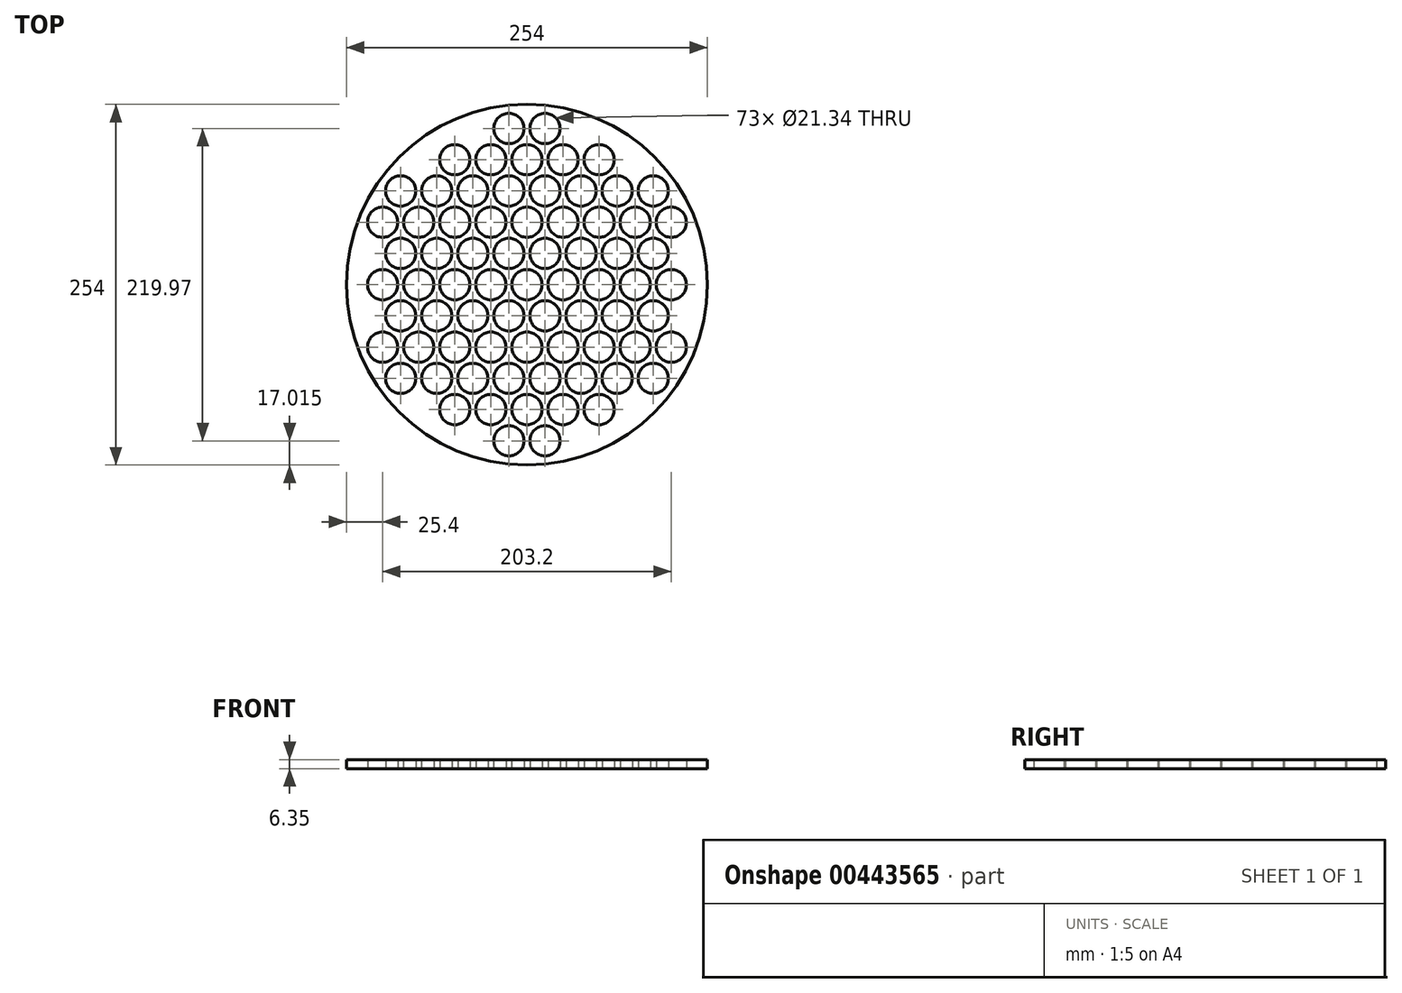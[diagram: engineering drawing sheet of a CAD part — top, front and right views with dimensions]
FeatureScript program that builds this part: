
annotation { "Feature Type Name" : "Feature", "Feature Type Description" : "" }
export const myFeature = defineFeature(function(context is Context, id is Id, definition is map)
    precondition{}
    {
        {
            var Q0;
            Q0=qCreatedBy(makeId("Top.planeOp"),FACE);
            var sketch = newSketch(context, id + "F0", { "sketchPlane" : qUnion([Q0])});
            skCircle(sketch, "E0", {"center": v(0, 0) * mm, "radius": 10.67 * mm});
            skCircle(sketch, "E1.1.0.0", {"center": v(25.4, 0) * mm, "radius": 10.67 * mm});
            skCircle(sketch, "E1.2.0.0", {"center": v(50.8, 0) * mm, "radius": 10.67 * mm});
            skLineSegment(sketch, "E1.direction1", {"start": v(0, 0) * mm, "end": v(25.4, 0) * mm, "construction": true});
            skCircle(sketch, "E2.0.3.0", {"center": v(76.2, 0) * mm, "radius": 10.67 * mm});
            skCircle(sketch, "E2.0.4.0", {"center": v(101.6, 0) * mm, "radius": 10.67 * mm});
            skCircle(sketch, "E3", {"center": v(12.7, 22) * mm, "radius": 10.67 * mm});
            skCircle(sketch, "E4.1.0.0", {"center": v(38.1, 22) * mm, "radius": 10.67 * mm});
            skCircle(sketch, "E4.2.0.0", {"center": v(63.5, 22) * mm, "radius": 10.67 * mm});
            skCircle(sketch, "E4.3.0.0", {"center": v(88.9, 22) * mm, "radius": 10.67 * mm});
            skLineSegment(sketch, "E4.direction1", {"start": v(12.7, 22) * mm, "end": v(38.1, 22) * mm, "construction": true});
            skCircle(sketch, "E5", {"center": v(0, 44) * mm, "radius": 10.67 * mm});
            skCircle(sketch, "E6.1.0.0", {"center": v(25.4, 44) * mm, "radius": 10.67 * mm});
            skCircle(sketch, "E6.2.0.0", {"center": v(50.8, 44) * mm, "radius": 10.67 * mm});
            skLineSegment(sketch, "E6.direction1", {"start": v(0, 44) * mm, "end": v(25.4, 44) * mm, "construction": true});
            skCircle(sketch, "E7.0.3.0", {"center": v(76.2, 44) * mm, "radius": 10.67 * mm});
            skCircle(sketch, "E7.0.4.0", {"center": v(101.6, 44) * mm, "radius": 10.67 * mm});
            skCircle(sketch, "E8", {"center": v(12.7, 66) * mm, "radius": 10.67 * mm});
            skCircle(sketch, "E9.1.0.0", {"center": v(38.1, 66) * mm, "radius": 10.67 * mm});
            skCircle(sketch, "E9.2.0.0", {"center": v(63.5, 66) * mm, "radius": 10.67 * mm});
            skCircle(sketch, "E9.3.0.0", {"center": v(88.9, 66) * mm, "radius": 10.67 * mm});
            skLineSegment(sketch, "E9.direction1", {"start": v(12.7, 66) * mm, "end": v(38.1, 66) * mm, "construction": true});
            skCircle(sketch, "E10", {"center": v(0, 0) * mm, "radius": 127 * mm});
            skCircle(sketch, "E11", {"center": v(0, 87.99) * mm, "radius": 10.67 * mm});
            skCircle(sketch, "E12.1.0.0", {"center": v(25.4, 87.99) * mm, "radius": 10.67 * mm});
            skCircle(sketch, "E12.2.0.0", {"center": v(50.8, 87.99) * mm, "radius": 10.67 * mm});
            skLineSegment(sketch, "E12.direction1", {"start": v(0, 87.99) * mm, "end": v(25.4, 87.99) * mm, "construction": true});
            skCircle(sketch, "E13", {"center": v(12.7, 109.99) * mm, "radius": 10.67 * mm});
            skLineSegment(sketch, "E14.direction1", {"start": v(12.7, 109.99) * mm, "end": v(38.1, 109.99) * mm, "construction": true});
            skCircle(sketch, "E15.MirrorC", {"center": v(-12.7, 66) * mm, "radius": 10.67 * mm});
            skLineSegment(sketch, "E16.MirrorCS", {"start": v(-12.7, 109.99) * mm, "end": v(-38.1, 109.99) * mm, "construction": true});
            skLineSegment(sketch, "E17.MirrorCS", {"start": v(-12.7, 66) * mm, "end": v(-38.1, 66) * mm, "construction": true});
            skCircle(sketch, "E18.MirrorC", {"center": v(-25.4, 87.99) * mm, "radius": 10.67 * mm});
            skCircle(sketch, "E19.MirrorC", {"center": v(-101.6, 44) * mm, "radius": 10.67 * mm});
            skCircle(sketch, "E20.MirrorC", {"center": v(-88.9, 66) * mm, "radius": 10.67 * mm});
            skCircle(sketch, "E21.MirrorC", {"center": v(-50.8, 87.99) * mm, "radius": 10.67 * mm});
            skLineSegment(sketch, "E22.MirrorCS", {"start": v(0, 44) * mm, "end": v(-25.4, 44) * mm, "construction": true});
            skCircle(sketch, "E23.MirrorC", {"center": v(-25.4, 44) * mm, "radius": 10.67 * mm});
            skCircle(sketch, "E24.MirrorC", {"center": v(-63.5, 66) * mm, "radius": 10.67 * mm});
            skCircle(sketch, "E25.MirrorC", {"center": v(-76.2, 44) * mm, "radius": 10.67 * mm});
            skLineSegment(sketch, "E26.MirrorCS", {"start": v(-12.7, 22) * mm, "end": v(-38.1, 22) * mm, "construction": true});
            skCircle(sketch, "E27.MirrorC", {"center": v(-25.4, 0) * mm, "radius": 10.67 * mm});
            skCircle(sketch, "E28.MirrorC", {"center": v(-38.1, 66) * mm, "radius": 10.67 * mm});
            skLineSegment(sketch, "E29.MirrorCS", {"start": v(0, 0) * mm, "end": v(-25.4, 0) * mm, "construction": true});
            skLineSegment(sketch, "E30.MirrorCS", {"start": v(0, 87.99) * mm, "end": v(-25.4, 87.99) * mm, "construction": true});
            skCircle(sketch, "E31.MirrorC", {"center": v(-38.1, 22) * mm, "radius": 10.67 * mm});
            skCircle(sketch, "E32.MirrorC", {"center": v(-76.2, 0) * mm, "radius": 10.67 * mm});
            skCircle(sketch, "E33.MirrorC", {"center": v(-50.8, 44) * mm, "radius": 10.67 * mm});
            skCircle(sketch, "E34.MirrorC", {"center": v(-101.6, 0) * mm, "radius": 10.67 * mm});
            skCircle(sketch, "E35.MirrorC", {"center": v(-50.8, 0) * mm, "radius": 10.67 * mm});
            skCircle(sketch, "E36.MirrorC", {"center": v(-12.7, 22) * mm, "radius": 10.67 * mm});
            skCircle(sketch, "E37.MirrorC", {"center": v(-12.7, 109.99) * mm, "radius": 10.67 * mm});
            skCircle(sketch, "E38.MirrorC", {"center": v(-63.5, 22) * mm, "radius": 10.67 * mm});
            skCircle(sketch, "E39.MirrorC", {"center": v(-88.9, 22) * mm, "radius": 10.67 * mm});
            skCircle(sketch, "E40.MirrorC", {"center": v(0, -87.99) * mm, "radius": 10.67 * mm});
            skLineSegment(sketch, "E41.MirrorCS", {"start": v(0, -44) * mm, "end": v(-25.4, -44) * mm, "construction": true});
            skCircle(sketch, "E42.MirrorC", {"center": v(0, -44) * mm, "radius": 10.67 * mm});
            skLineSegment(sketch, "E43.MirrorCS", {"start": v(0, -87.99) * mm, "end": v(-25.4, -87.99) * mm, "construction": true});
            skLineSegment(sketch, "E44.MirrorCS", {"start": v(-12.7, -66) * mm, "end": v(-38.1, -66) * mm, "construction": true});
            skCircle(sketch, "E45.MirrorC", {"center": v(12.7, -66) * mm, "radius": 10.67 * mm});
            skCircle(sketch, "E46.MirrorC", {"center": v(25.4, -87.99) * mm, "radius": 10.67 * mm});
            skCircle(sketch, "E47.MirrorC", {"center": v(-50.8, -87.99) * mm, "radius": 10.67 * mm});
            skLineSegment(sketch, "E48.MirrorCS", {"start": v(-12.7, -109.99) * mm, "end": v(-38.1, -109.99) * mm, "construction": true});
            skCircle(sketch, "E49.MirrorC", {"center": v(101.6, -44) * mm, "radius": 10.67 * mm});
            skCircle(sketch, "E50.MirrorC", {"center": v(-50.8, -44) * mm, "radius": 10.67 * mm});
            skCircle(sketch, "E51.MirrorC", {"center": v(-12.7, -66) * mm, "radius": 10.67 * mm});
            skCircle(sketch, "E52.MirrorC", {"center": v(76.2, -44) * mm, "radius": 10.67 * mm});
            skCircle(sketch, "E53.MirrorC", {"center": v(63.5, -22) * mm, "radius": 10.67 * mm});
            skCircle(sketch, "E54.MirrorC", {"center": v(-76.2, -44) * mm, "radius": 10.67 * mm});
            skCircle(sketch, "E55.MirrorC", {"center": v(50.8, -87.99) * mm, "radius": 10.67 * mm});
            skCircle(sketch, "E56.MirrorC", {"center": v(12.7, -22) * mm, "radius": 10.67 * mm});
            skCircle(sketch, "E57.MirrorC", {"center": v(38.1, -66) * mm, "radius": 10.67 * mm});
            skCircle(sketch, "E58.MirrorC", {"center": v(-38.1, -22) * mm, "radius": 10.67 * mm});
            skLineSegment(sketch, "E59.MirrorCS", {"start": v(12.7, -66) * mm, "end": v(38.1, -66) * mm, "construction": true});
            skLineSegment(sketch, "E60.MirrorCS", {"start": v(-12.7, -22) * mm, "end": v(-38.1, -22) * mm, "construction": true});
            skLineSegment(sketch, "E61.MirrorCS", {"start": v(12.7, -109.99) * mm, "end": v(38.1, -109.99) * mm, "construction": true});
            skCircle(sketch, "E62.MirrorC", {"center": v(50.8, -44) * mm, "radius": 10.67 * mm});
            skCircle(sketch, "E63.MirrorC", {"center": v(-38.1, -66) * mm, "radius": 10.67 * mm});
            skCircle(sketch, "E64.MirrorC", {"center": v(-25.4, -44) * mm, "radius": 10.67 * mm});
            skCircle(sketch, "E65.MirrorC", {"center": v(-12.7, -22) * mm, "radius": 10.67 * mm});
            skLineSegment(sketch, "E66.MirrorCS", {"start": v(12.7, -22) * mm, "end": v(38.1, -22) * mm, "construction": true});
            skCircle(sketch, "E67.MirrorC", {"center": v(88.9, -22) * mm, "radius": 10.67 * mm});
            skCircle(sketch, "E68.MirrorC", {"center": v(38.1, -22) * mm, "radius": 10.67 * mm});
            skCircle(sketch, "E69.MirrorC", {"center": v(88.9, -66) * mm, "radius": 10.67 * mm});
            skCircle(sketch, "E70.MirrorC", {"center": v(-63.5, -66) * mm, "radius": 10.67 * mm});
            skCircle(sketch, "E71.MirrorC", {"center": v(25.4, -44) * mm, "radius": 10.67 * mm});
            skCircle(sketch, "E72.MirrorC", {"center": v(-12.7, -109.99) * mm, "radius": 10.67 * mm});
            skCircle(sketch, "E73.MirrorC", {"center": v(-88.9, -22) * mm, "radius": 10.67 * mm});
            skCircle(sketch, "E74.MirrorC", {"center": v(-25.4, -87.99) * mm, "radius": 10.67 * mm});
            skCircle(sketch, "E75.MirrorC", {"center": v(12.7, -109.99) * mm, "radius": 10.67 * mm});
            skCircle(sketch, "E76.MirrorC", {"center": v(-63.5, -22) * mm, "radius": 10.67 * mm});
            skCircle(sketch, "E77.MirrorC", {"center": v(-101.6, -44) * mm, "radius": 10.67 * mm});
            skCircle(sketch, "E78.MirrorC", {"center": v(-88.9, -66) * mm, "radius": 10.67 * mm});
            skLineSegment(sketch, "E79.MirrorCS", {"start": v(0, -87.99) * mm, "end": v(25.4, -87.99) * mm, "construction": true});
            skLineSegment(sketch, "E80.MirrorCS", {"start": v(0, -44) * mm, "end": v(25.4, -44) * mm, "construction": true});
            skCircle(sketch, "E81.MirrorC", {"center": v(63.5, -66) * mm, "radius": 10.67 * mm});
            skSolve(sketch);
        }
        {
            var Q0;
            Q0 = qSketchRegion(id + "F0", true);
            extrude(context, id + "F1", {"entities" : qUnion([Q0]), "depth" : 6.35 * mm});
        }
    });
